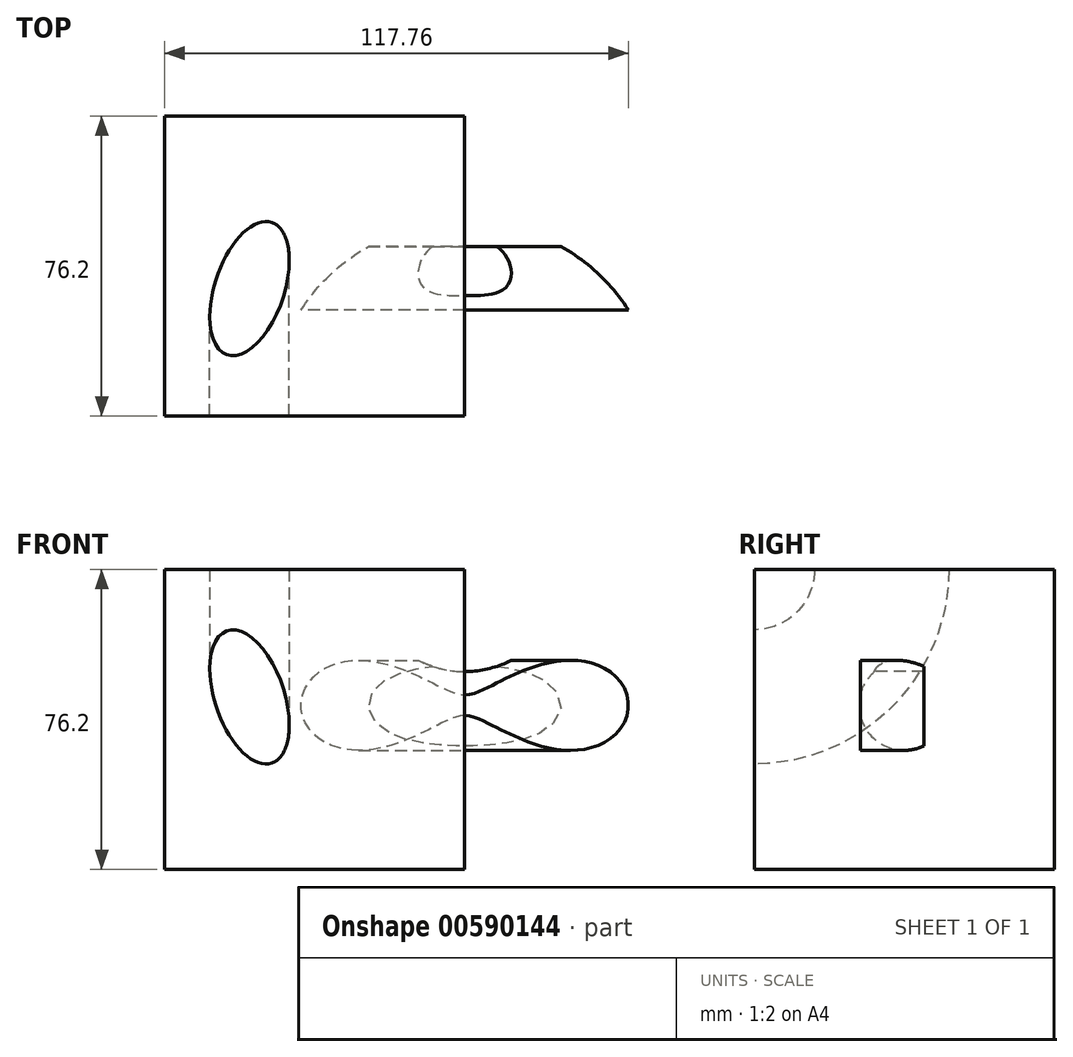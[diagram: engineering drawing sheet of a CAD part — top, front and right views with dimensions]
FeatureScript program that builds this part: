
annotation { "Feature Type Name" : "Feature", "Feature Type Description" : "" }
export const myFeature = defineFeature(function(context is Context, id is Id, definition is map)
    precondition{}
    {
        {
            var Q0;
            Q0=qCreatedBy(makeId("Front.planeOp"),FACE);
            var sketch = newSketch(context, id + "F0", { "sketchPlane" : qUnion([Q0])});
            skLineSegment(sketch, "E0.bottom", {"start": v(0, 0) * mm, "end": v(76.2, 0) * mm});
            skLineSegment(sketch, "E0.top", {"start": v(0, 76.2) * mm, "end": v(76.2, 76.2) * mm});
            skLineSegment(sketch, "E0.left", {"start": v(0, 0) * mm, "end": v(0, 76.2) * mm});
            skLineSegment(sketch, "E0.right", {"start": v(76.2, 0) * mm, "end": v(76.2, 76.2) * mm});
            skSolve(sketch);
        }
        {
            var Q0;
            Q0 = qSketchRegion(id + "F0", true);
            extrude(context, id + "F1", {"entities" : qUnion([Q0]), "depth" : 76.2 * mm, "offsetDistance" : 25.4 * mm});
        }
        {
            var Q0;
            Q0=makeQuery(id+"F1.opExtrude","CAP_FACE",FACE,{"disambiguationData":[OSD([sQuery(id+"F0.wireOp",EDGE,"E0.bottom"),sQuery(id+"F0.wireOp",EDGE,"E0.top"),sQuery(id+"F0.wireOp",EDGE,"E0.left"),sQuery(id+"F0.wireOp",EDGE,"E0.right")])],"isStart":false});
            var sketch = newSketch(context, id + "F2", { "sketchPlane" : qUnion([Q0])});
            skEllipse(sketch, "E1", {"center": v(21.52, 43.84) * mm, "majorRadius": 17.74 * mm, "minorRadius": 8.81 * mm, "majorAxis": v(0.32, -0.95)});
            skSolve(sketch);
        }
        {
            var Q0;
            Q0=makeQuery(id+"F1.opExtrude","SWEPT_FACE",FACE,{"disambiguationData":[OSD([sQuery(id+"F0.wireOp",EDGE,"E0.right")])]});
            var sketch = newSketch(context, id + "F3", { "sketchPlane" : qUnion([Q0])});
            skLineSegment(sketch, "E2.bottom", {"start": v(-49.22, 50.27) * mm, "end": v(-33.1, 50.27) * mm});
            skLineSegment(sketch, "E2.top", {"start": v(-49.22, 16.65) * mm, "end": v(-33.1, 16.65) * mm});
            skLineSegment(sketch, "E2.left", {"start": v(-49.22, 50.27) * mm, "end": v(-49.22, 16.65) * mm});
            skLineSegment(sketch, "E2.right", {"start": v(-33.1, 50.27) * mm, "end": v(-33.1, 16.65) * mm});
            skSolve(sketch);
        }
        {
            var Q0;
            Q0=makeQuery(id+"F3.imprint","IMPRINT",FACE,{"disambiguationData":[TD([[makeQuery(id+"F3.imprint","IMPRINT",EDGE,{"derivedFrom":sQuery(id+"F3.wireOp",EDGE,"E2.bottom")}),-1.0]])]});
            var Q1;
            Q1=makeQuery(id+"F1.opExtrude","SWEPT_EDGE",EDGE,{"disambiguationData":[OSD([sQuery(id+"F0.wireOp",EDGE,"E0.top"),sQuery(id+"F0.wireOp",EDGE,"E0.right")])]});
            revolve(context, id + "F4", {"entities" : qUnion([Q0]), "axis" : qUnion([Q1]), "revolveType" : RevolveType.FULL});
        }
        {
            var Q0;
            Q0=makeQuery(id+"F1.opExtrude","CAP_FACE",FACE,{"disambiguationData":[OSD([sQuery(id+"F0.wireOp",EDGE,"E0.bottom"),sQuery(id+"F0.wireOp",EDGE,"E0.top"),sQuery(id+"F0.wireOp",EDGE,"E0.left"),sQuery(id+"F0.wireOp",EDGE,"E0.right")])],"isStart":false});
            var sketch = newSketch(context, id + "F5", { "sketchPlane" : qUnion([Q0])});
            skCircle(sketch, "E3", {"center": v(38.09, 41.7) * mm, "radius": 11.44 * mm});
            skSolve(sketch);
        }
        {
            var Q0;
            Q0=makeQuery(id+"F5.imprint","IMPRINT",FACE,{"disambiguationData":[TD([[makeQuery(id+"F5.imprint","IMPRINT",EDGE,{"derivedFrom":sQuery(id+"F5.wireOp",EDGE,"E3")}),1.0]])]});
            var Q1;
            Q1=makeQuery(id+"F1.opExtrude","CAP_EDGE",EDGE,{"disambiguationData":[OSD([sQuery(id+"F0.wireOp",EDGE,"E0.right")])],"isStart":false});
            revolve(context, id + "F6", {"entities" : qUnion([Q0]), "axis" : qUnion([Q1]), "revolveType" : RevolveType.FULL});
        }
        {
            var Q0;
            Q0=makeQuery(id+"F2.imprint","IMPRINT",FACE,{"disambiguationData":[TD([[makeQuery(id+"F2.imprint","IMPRINT",EDGE,{"derivedFrom":sQuery(id+"F2.wireOp",EDGE,"E1")}),1.0]])]});
            var Q1;
            Q1=makeQuery(id+"F1.opExtrude","CAP_EDGE",EDGE,{"disambiguationData":[OSD([sQuery(id+"F0.wireOp",EDGE,"E0.top")])],"isStart":false});
            revolve(context, id + "F7", {"entities" : qUnion([Q0]), "axis" : qUnion([Q1]), "revolveType" : RevolveType.FULL});
        }
        {
            var Q0;
            Q0=makeQuery(id+"F7.opRevolve","SWEPT_BODY",BODY,{"disambiguationData":[OSD([sQuery(id+"F2.wireOp",EDGE,"E1")])]});
            var Q1;
            Q1=makeQuery(id+"F1.opExtrude","SWEPT_BODY",BODY,{"disambiguationData":[OSD([sQuery(id+"F0.wireOp",EDGE,"E0.bottom"),sQuery(id+"F0.wireOp",EDGE,"E0.top"),sQuery(id+"F0.wireOp",EDGE,"E0.left"),sQuery(id+"F0.wireOp",EDGE,"E0.right")])]});
            var Q2;
            Q2=makeQuery(id+"F4.opRevolve","SWEPT_BODY",BODY,{"disambiguationData":[OSD([sQuery(id+"F3.wireOp",EDGE,"E2.bottom"),sQuery(id+"F3.wireOp",EDGE,"E2.top"),sQuery(id+"F3.wireOp",EDGE,"E2.left"),sQuery(id+"F3.wireOp",EDGE,"E2.right")])]});
            booleanBodies(context, id + "F8", {"operationType" : BooleanOperationType.SUBTRACTION, "tools" : qUnion([Q0]), "targets" : qUnion([Q1, Q2])});
        }
        {
            var Q0;
            Q0=makeQuery(id+"F4.opRevolve","SWEPT_BODY",BODY,{"disambiguationData":[OSD([sQuery(id+"F3.wireOp",EDGE,"E2.bottom"),sQuery(id+"F3.wireOp",EDGE,"E2.top"),sQuery(id+"F3.wireOp",EDGE,"E2.left"),sQuery(id+"F3.wireOp",EDGE,"E2.right")])]});
            var Q1;
            Q1=makeQuery(id+"F6.opRevolve","SWEPT_BODY",BODY,{"disambiguationData":[OSD([sQuery(id+"F5.wireOp",EDGE,"E3")])]});
            booleanBodies(context, id + "F9", {"operationType" : BooleanOperationType.INTERSECTION, "tools" : qUnion([Q0, Q1])});
        }
    });
